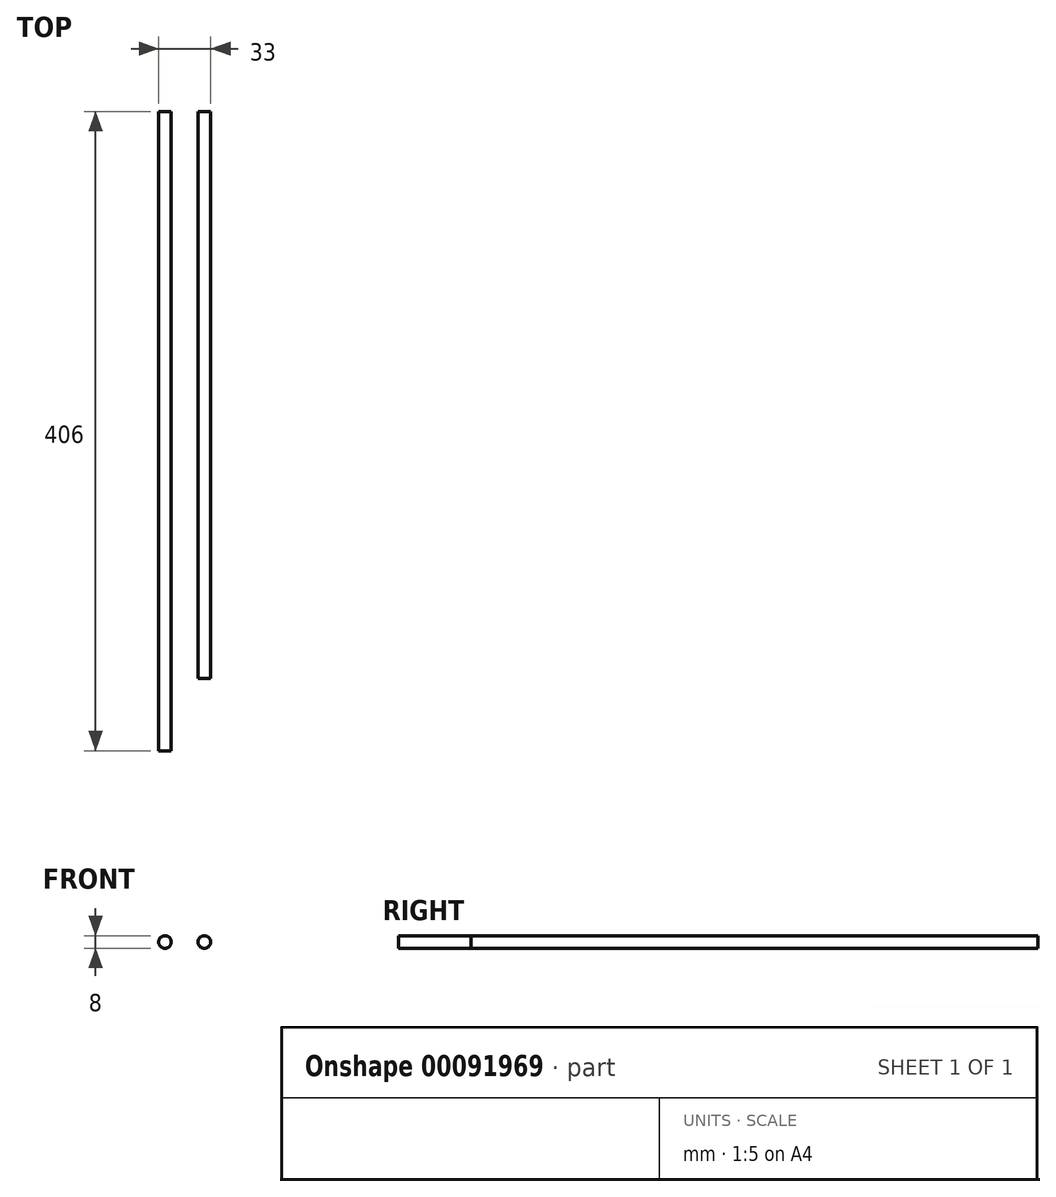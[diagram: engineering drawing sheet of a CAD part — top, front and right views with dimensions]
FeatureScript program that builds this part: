
annotation { "Feature Type Name" : "Feature", "Feature Type Description" : "" }
export const myFeature = defineFeature(function(context is Context, id is Id, definition is map)
    precondition{}
    {
        {
            var Q0;
            Q0=qCreatedBy(makeId("Front.planeOp"),FACE);
            var sketch = newSketch(context, id + "F0", { "sketchPlane" : qUnion([Q0])});
            skCircle(sketch, "E0", {"center": v(0, 0) * mm, "radius": 4 * mm});
            skCircle(sketch, "E1.1.0.0", {"center": v(25, 0) * mm, "radius": 4 * mm});
            skLineSegment(sketch, "E1.direction1", {"start": v(0, 0) * mm, "end": v(25, 0) * mm, "construction": true});
            skSolve(sketch);
        }
        {
            var Q0;
            Q0=makeQuery(id+"F0.imprint","IMPRINT",FACE,{"disambiguationData":[TD([[makeQuery(id+"F0.imprint","IMPRINT",EDGE,{"derivedFrom":sQuery(id+"F0.wireOp",EDGE,"E0")}),1.0]])]});
            extrude(context, id + "F1", {"entities" : qUnion([Q0]), "depth" : 406 * mm});
        }
        {
            var Q0;
            Q0=makeQuery(id+"F0.imprint","IMPRINT",FACE,{"disambiguationData":[TD([[makeQuery(id+"F0.imprint","IMPRINT",EDGE,{"derivedFrom":sQuery(id+"F0.wireOp",EDGE,"E1.1.0.0")}),1.0]])]});
            extrude(context, id + "F2", {"entities" : qUnion([Q0]), "depth" : 360 * mm});
        }
    });
